# Revit family: 2093085 Lighting Fixture_Sylvania_Unity Micro Prism Diffuser 3000K White_Ceiling Pendant
name_source: partatom
category: Lighting Fixtures
revit_build: Autodesk Revit 2017 (Build: 20190507_1515(x64)
units: mm (PartAtom-declared; Revit-internal decimal feet)

## family parameters
Cut with Voids When Loaded = No
Host = Face
Light Source = Yes
OmniClass Number = 23.80.70.11.17
OmniClass Title = Specialized Lighting by Location or Use
Part Type = Normal
Room Calculation Point = No
Round Connector Dimension = Use Diameter
Shared = No

## types (1)
- UNITY2 1.2M 3000K DALI EMPRO WHITE
    Apparent Load = 39 VA
    Assembly Code = D5020200
    Body Material = Aluminum_Sylvania_Unity_White 9016
    CRI ( Ra ) = 80
    Catalog Number = 2093085 UNITY2 1.2M 3000K DALI EMPRO WHITE
    Color Filter = 16777215
    Default Elevation = 0 mm  [stored 0 ft]
    Description = Versatile suspended modular LED linear system. Install horizontally or down stairwells using pivot accessories. Create innovative lighting runs or spatial frameworks for open plan offices, corridors, classrooms or libraries. Bi-directional lighting - 70% downwards and 30% upwards. 1.2m, 2.4m and 3.6m aluminium extrusions - ‘mix and match’ differing lengths to create a perfect lighting system. Rapid connector kit accessory - allowing for quick through wired installations of continuous straight runs. Sensor modules - control light through ‘daylight harvesting’ via Organic Response technology or standard PIR. UGR <19. DALI, 3 hour emergency and EMPRO versions available
    Diffuser Material = Polycarbonate_Sylvania_Unity_Clear
    Diffuser Number = 2
    Dimming Lamp Color Temperature Shift = <None>
    Distribution Type = Direct/Indirect
    Drive Current = 1050 mA
    Electrical Protection = Class I
    Emit Shape Visible in Rendering = No
    Emit from Rectangle Length = 1201.4 mm  [stored 3.9416 ft]
    Emit from Rectangle Width = 43.2 mm
    Glow Wire Test = 960 °C
    Height = 56.2 mm  [stored 0.184383 ft]
    IP Rating = IP20
    LOR = 100%
    Lamp = 39W
    Lamp Comments = LED
    Lamp Material = Acrylic High Luminance Glass_Sylvania_Unity_White
    Length = 1256 mm
    Life = 50 000 h
    Manufacturer = Feilo Sylvania
    Model = UNITY2 1.2M 3000K DALI EMPRO WHITE
    Mounting Height = 1000 mm  [stored 3.28084 ft]
    Photometric Web File = 2093085_UNITY21.2M3KDALIEMPROWHT-201370.ies
    Product Family = UNITY2 1.2M 3K DALI WHT - 3000K (WHITE)
    Product Page URL = http://www.sylvania-lighting.com
    Reflector Material = Aluminum_Sylvania_Unity_Silver
    Rod Material = Stainless Steel_Sylvania_Unity_Grey
    Rods Number = 2
    Tilt Angle = -90.00°
    Top Cap Length = 1201.4 mm  [stored 3.9416 ft]
    UGR = <19
    URL = http://www.sylvania-lighting.com
    Voltage = 230 V
    Voltage Comments = UNV (Universal Voltage; 230-240 Volt)
    Weight = 3.32 kg
    Width = 138 mm  [stored 0.452756 ft]

note: [stored X ft] marks values corroborated as IEEE doubles in the binary element streams (Revit-internal decimal feet)

## geometry (parser evidence)
native form markers: Blend x8, Sweep x10
no freeform markers — native parametric forms only
